# Revit family: RAPID20G
name_source: partatom
category: Generic Models
revit_build: Autodesk Revit LT 2017 (Build: 20170118_1100(x64)
units: mm (PartAtom-declared; Revit-internal decimal feet)

## family parameters
Always vertical = No
Can host rebar = No
Cut with Voids When Loaded = No
Part Type = Normal
Room Calculation Point = No
Round Connector Dimension = Use Diameter
Shared = No
Work Plane-Based = Yes

## types (1)
- NBS Standard Parameters
    AssetType = Fixed
    BIMObjectName = Metpro_Metprolibrary_Conduitfittings_Metalcomponent_Steelaccessories
    Color = Grey
    Default Elevation = 1219 mm
    Description = RAPID20G - 20mm Rapid Saddle
    DurationUnit = 1 Year
    Finish = Delta Protekt
    Manufacturer = Metpro Limited
    ManufacturerName = Metpro ltd
    ManufacturerURL = www.metpro.co.uk
    Material = Pressed Steel
    ModelNumber = RAPID20G
    ModelReference = Conduit Fittings
    NBSDescription = Conduit Fittings
    NBSReference = 90-55-10/460
    Name = RAPID20 - RAPID SADDLE
    NominalHeight = 23 mm
    NominalLength = 57 mm
    NominalWidth = 22 mm
    ProductInformation = www.metpro.co.uk/pdf/rapid20G.pdf
    Size = 20mm
    URL = www.metpro.co.uk
    Uniclass2 = Pr_65_70_11_20
    Version = 1
    WarrantyDurationUnit = 12 Months
    WarrantyGuarantorParts = 12 Months
    Weight = 0.0195kg

## geometry (parser evidence)
native form markers: Sweep x1
no freeform markers — native parametric forms only
